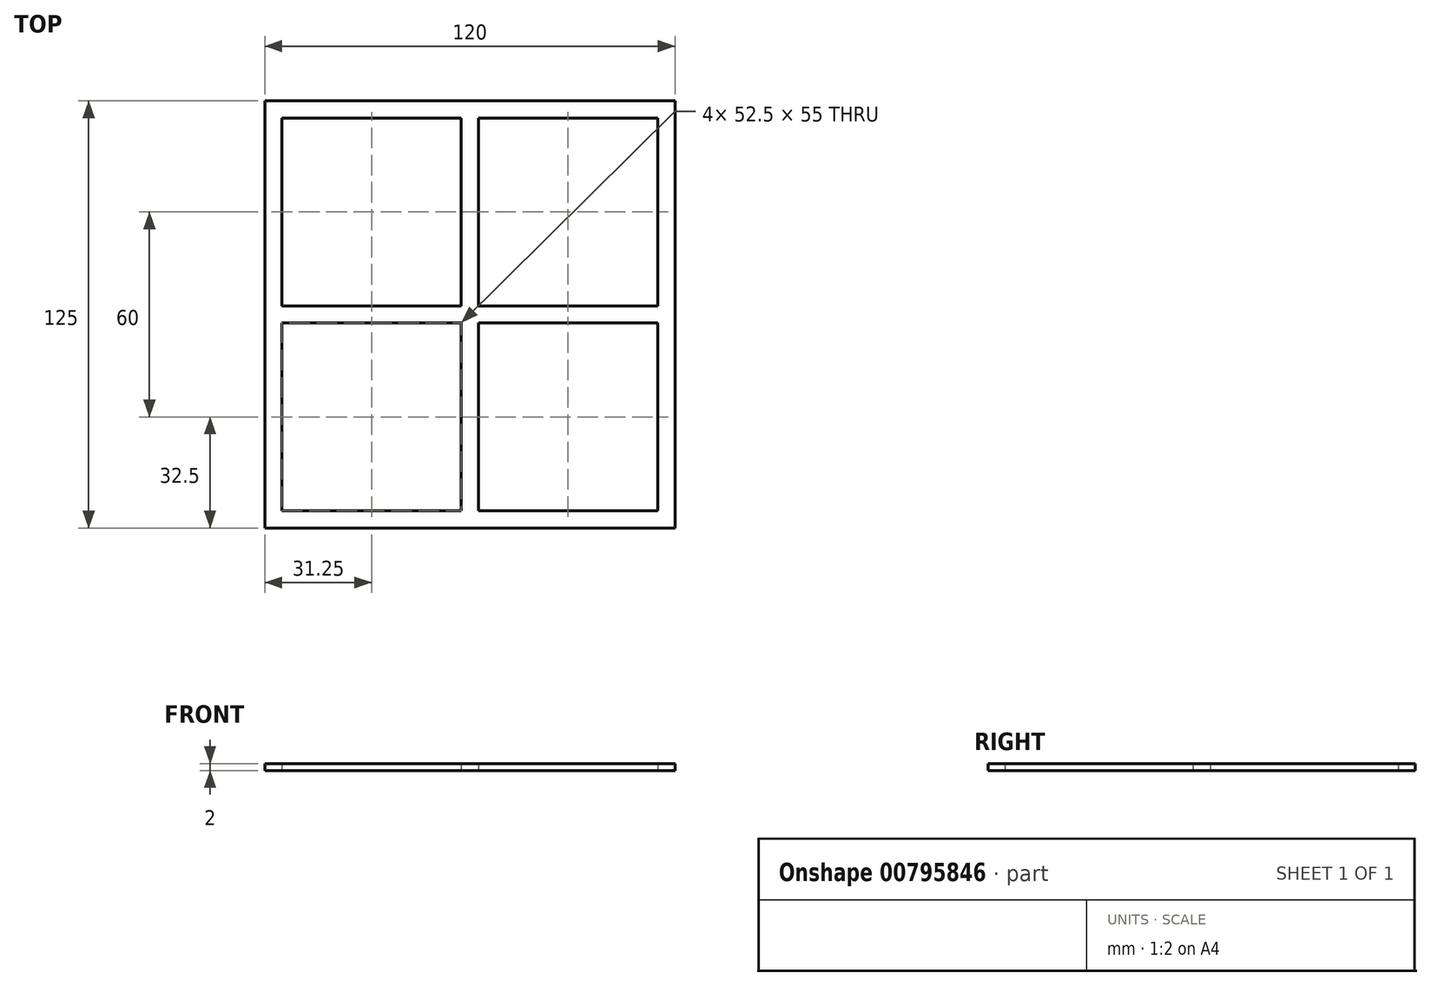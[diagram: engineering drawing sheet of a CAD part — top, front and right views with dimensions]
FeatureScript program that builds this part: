
annotation { "Feature Type Name" : "Feature", "Feature Type Description" : "" }
export const myFeature = defineFeature(function(context is Context, id is Id, definition is map)
    precondition{}
    {
        {
            var Q0;
            Q0=qCreatedBy(makeId("Top.planeOp"),FACE);
            var sketch = newSketch(context, id + "F0", { "sketchPlane" : qUnion([Q0])});
            skLineSegment(sketch, "E0.bottom", {"start": v(60, -62.5) * mm, "end": v(-60, -62.5) * mm});
            skLineSegment(sketch, "E0.top", {"start": v(60, 62.5) * mm, "end": v(-60, 62.5) * mm});
            skLineSegment(sketch, "E0.left", {"start": v(60, -62.5) * mm, "end": v(60, 62.5) * mm});
            skLineSegment(sketch, "E0.right", {"start": v(-60, -62.5) * mm, "end": v(-60, 62.5) * mm});
            skPoint(sketch, "E0.middle", {"position": v(0, 0) * mm});
            skLineSegment(sketch, "E1.0", {"start": v(55, -57.5) * mm, "end": v(2.5, -57.5) * mm});
            skLineSegment(sketch, "E1.1", {"start": v(55, -57.5) * mm, "end": v(55, -2.5) * mm});
            skLineSegment(sketch, "E1.2", {"start": v(55, 57.5) * mm, "end": v(2.5, 57.5) * mm});
            skLineSegment(sketch, "E1.3", {"start": v(-55, -57.5) * mm, "end": v(-55, -2.5) * mm});
            skLineSegment(sketch, "E2", {"start": v(2.5, -57.5) * mm, "end": v(2.5, -2.5) * mm});
            skLineSegment(sketch, "E3.MirrorCS", {"start": v(-2.5, -57.5) * mm, "end": v(-2.5, -2.5) * mm});
            skLineSegment(sketch, "E4", {"start": v(-55, -2.5) * mm, "end": v(-2.5, -2.5) * mm});
            skLineSegment(sketch, "E5.MirrorCS", {"start": v(-55, 2.5) * mm, "end": v(-2.5, 2.5) * mm});
            skLineSegment(sketch, "E6.trimOffspring", {"start": v(-2.5, 57.5) * mm, "end": v(-55, 57.5) * mm});
            skLineSegment(sketch, "E7.trimOffspring", {"start": v(2.5, 2.5) * mm, "end": v(55, 2.5) * mm});
            skLineSegment(sketch, "E8.trimOffspring", {"start": v(2.5, 2.5) * mm, "end": v(2.5, 57.5) * mm});
            skLineSegment(sketch, "E9.trimOffspring", {"start": v(2.5, -2.5) * mm, "end": v(55, -2.5) * mm});
            skLineSegment(sketch, "E10.trimOffspring", {"start": v(-2.5, 2.5) * mm, "end": v(-2.5, 57.5) * mm});
            skLineSegment(sketch, "E11.trimOffspring", {"start": v(55, 2.5) * mm, "end": v(55, 57.5) * mm});
            skLineSegment(sketch, "E12.trimOffspring", {"start": v(-55, 2.5) * mm, "end": v(-55, 57.5) * mm});
            skLineSegment(sketch, "E13.trimOffspring", {"start": v(-2.5, -57.5) * mm, "end": v(-55, -57.5) * mm});
            skSolve(sketch);
        }
        {
            var Q0;
            Q0 = qSketchRegion(id + "F0", true);
            extrude(context, id + "F1", {"entities" : qUnion([Q0]), "depth" : 2 * mm, "offsetDistance" : 25 * mm});
        }
    });
